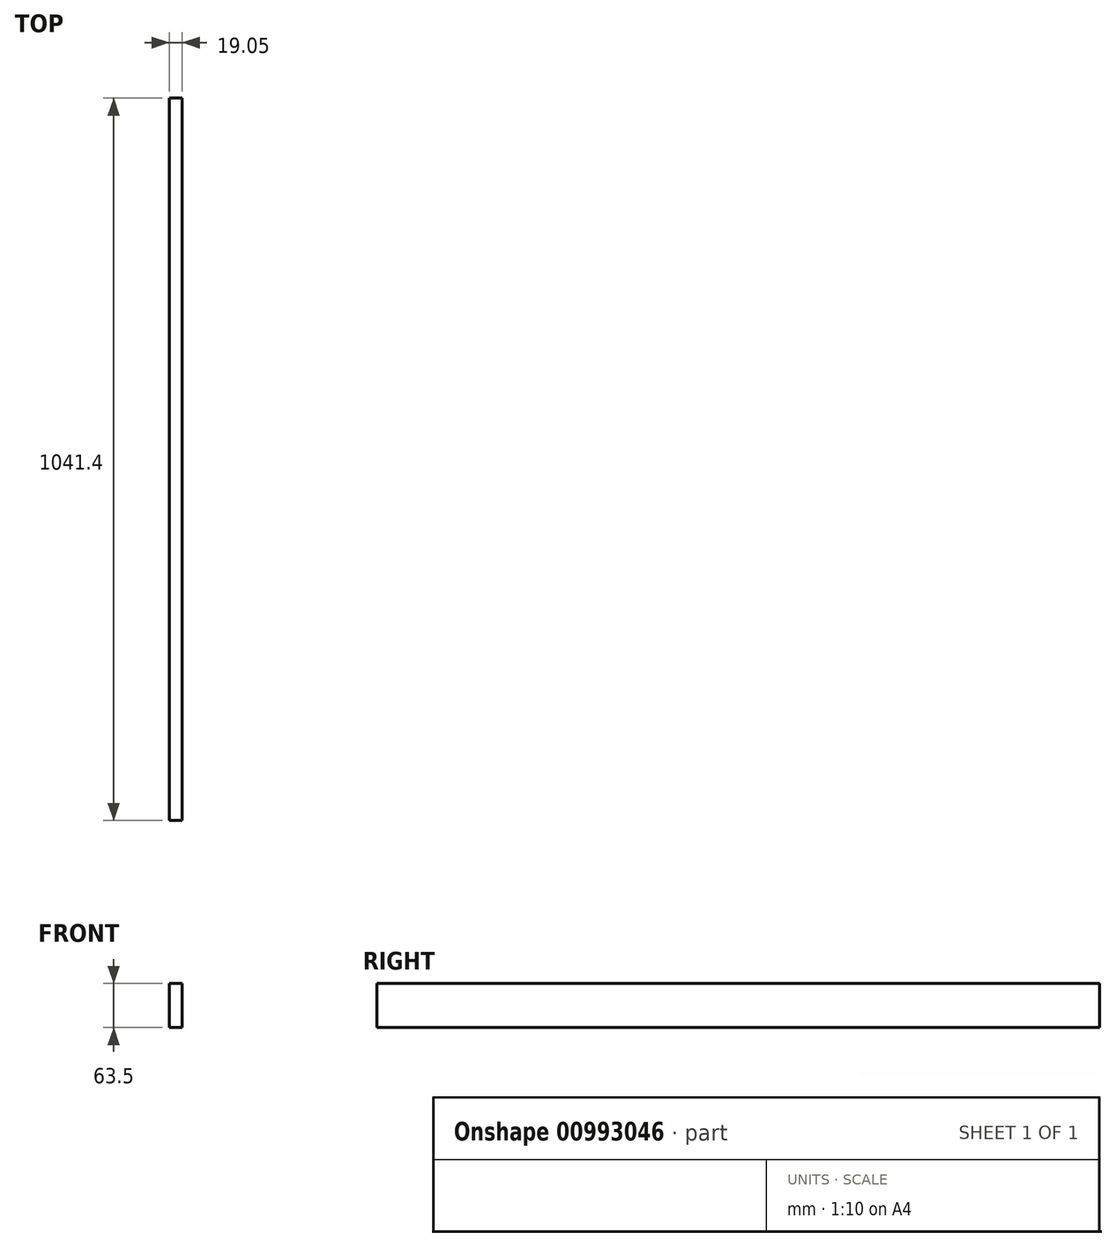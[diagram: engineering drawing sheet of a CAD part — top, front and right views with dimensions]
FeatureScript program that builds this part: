
annotation { "Feature Type Name" : "Feature", "Feature Type Description" : "" }
export const myFeature = defineFeature(function(context is Context, id is Id, definition is map)
    precondition{}
    {
        {
            var Q0;
            Q0=qCreatedBy(makeId("Front.planeOp"),FACE);
            var sketch = newSketch(context, id + "F0", { "sketchPlane" : qUnion([Q0])});
            skLineSegment(sketch, "E0.bottom", {"start": v(-19.05, 72.41) * mm, "end": v(0, 72.41) * mm});
            skLineSegment(sketch, "E0.top", {"start": v(-19.05, 8.91) * mm, "end": v(0, 8.91) * mm});
            skLineSegment(sketch, "E0.left", {"start": v(-19.05, 72.41) * mm, "end": v(-19.05, 8.91) * mm});
            skLineSegment(sketch, "E0.right", {"start": v(0, 72.41) * mm, "end": v(0, 8.91) * mm});
            skSolve(sketch);
        }
        {
            var Q0;
            Q0 = qSketchRegion(id + "F0", true);
            extrude(context, id + "F1", {"entities" : qUnion([Q0]), "endBound" : BoundingType.SYMMETRIC, "depth" : 1041.4 * mm, "offsetDistance" : 25.4 * mm});
        }
    });
